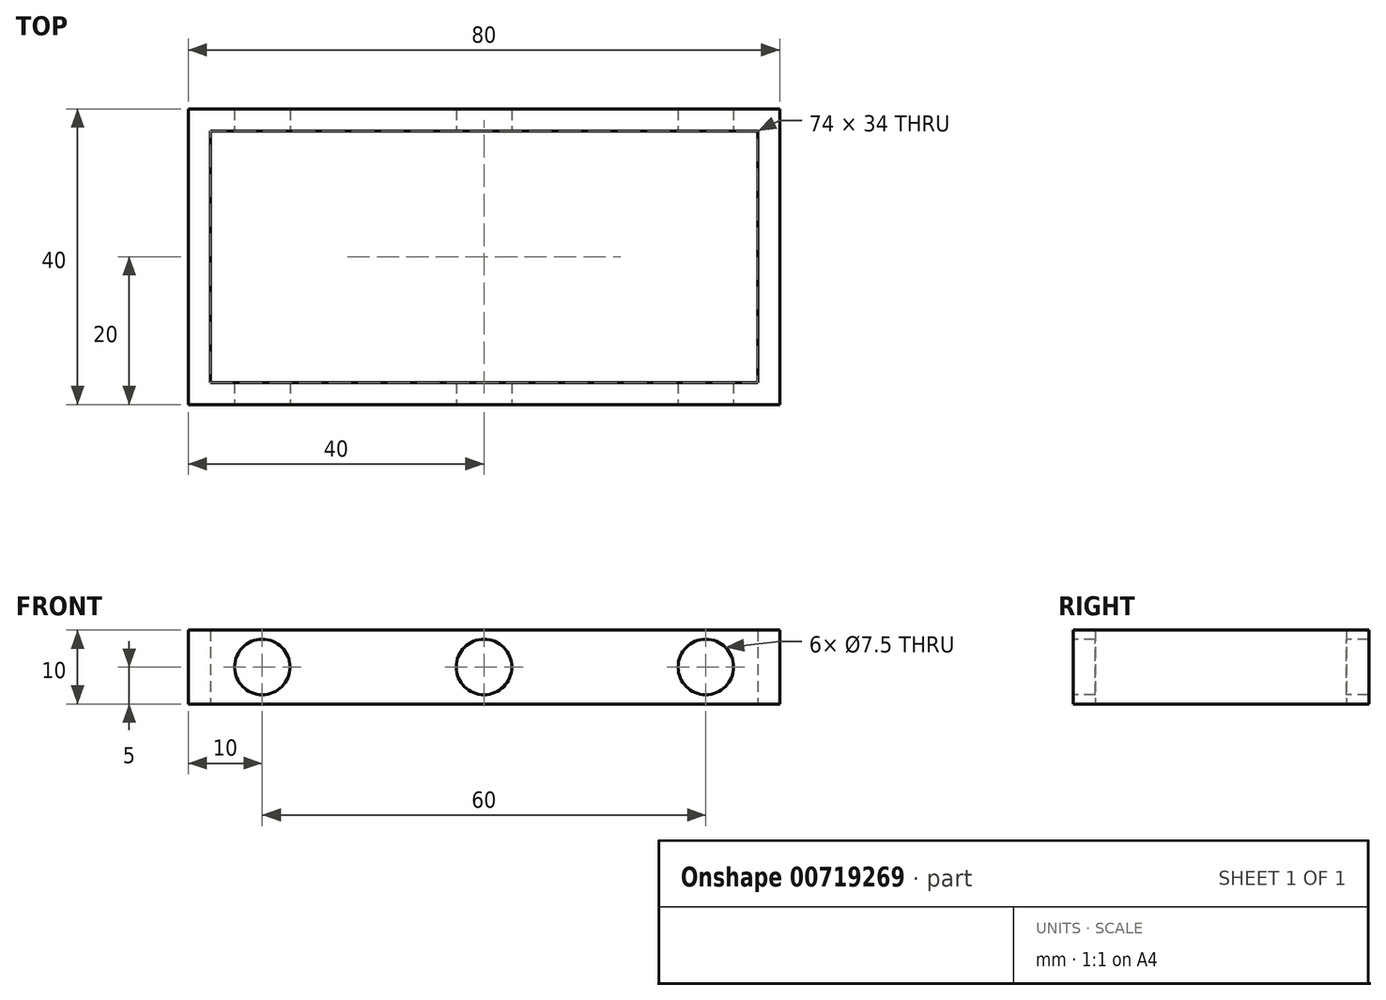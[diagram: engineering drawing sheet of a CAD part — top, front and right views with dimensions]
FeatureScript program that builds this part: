
annotation { "Feature Type Name" : "Feature", "Feature Type Description" : "" }
export const myFeature = defineFeature(function(context is Context, id is Id, definition is map)
    precondition{}
    {
        {
            var Q0;
            Q0=qCreatedBy(makeId("Front.planeOp"),FACE);
            var sketch = newSketch(context, id + "F0", { "sketchPlane" : qUnion([Q0])});
            skLineSegment(sketch, "E0.bottom", {"start": v(-40, 5) * mm, "end": v(40, 5) * mm});
            skLineSegment(sketch, "E0.top", {"start": v(-40, -5) * mm, "end": v(40, -5) * mm});
            skLineSegment(sketch, "E0.left", {"start": v(-40, 5) * mm, "end": v(-40, -5) * mm});
            skLineSegment(sketch, "E0.right", {"start": v(40, 5) * mm, "end": v(40, -5) * mm});
            skSolve(sketch);
        }
        {
            var Q0;
            Q0=makeQuery(id+"F0.imprint","IMPRINT",FACE,{"disambiguationData":[TD([[makeQuery(id+"F0.imprint","IMPRINT",EDGE,{"derivedFrom":sQuery(id+"F0.wireOp",EDGE,"E0.bottom")}),-1.0]])]});
            extrude(context, id + "F1", {"entities" : qUnion([Q0]), "depth" : 40 * mm, "offsetDistance" : 25 * mm, "symmetric" : true});
        }
        {
            var Q0;
            Q0=makeQuery(id+"F1.opExtrude","SWEPT_FACE",FACE,{"disambiguationData":[OSD([sQuery(id+"F0.wireOp",EDGE,"E0.bottom")])]});
            var Q1;
            Q1=makeQuery(id+"F1.opExtrude","SWEPT_FACE",FACE,{"disambiguationData":[OSD([sQuery(id+"F0.wireOp",EDGE,"E0.top")])]});
            shell(context, id + "F2", {"entities" : qUnion([Q0, Q1]), "thickness" : 3 * mm});
        }
        {
            var Q0;
            Q0=qCreatedBy(makeId("Front.planeOp"),FACE);
            var sketch = newSketch(context, id + "F3", { "sketchPlane" : qUnion([Q0])});
            skCircle(sketch, "E1", {"center": v(-30, 0) * mm, "radius": 3.75 * mm});
            skCircle(sketch, "E2", {"center": v(0, 0) * mm, "radius": 3.75 * mm});
            skCircle(sketch, "E3", {"center": v(30, 0) * mm, "radius": 3.75 * mm});
            skSolve(sketch);
        }
        {
            var Q0;
            Q0=makeQuery(id+"F3.imprint","IMPRINT",FACE,{"disambiguationData":[TD([[makeQuery(id+"F3.imprint","IMPRINT",EDGE,{"derivedFrom":sQuery(id+"F3.wireOp",EDGE,"E1")}),1.0]])]});
            var Q1;
            Q1=makeQuery(id+"F3.imprint","IMPRINT",FACE,{"disambiguationData":[TD([[makeQuery(id+"F3.imprint","IMPRINT",EDGE,{"derivedFrom":sQuery(id+"F3.wireOp",EDGE,"E2")}),1.0]])]});
            var Q2;
            Q2=makeQuery(id+"F3.imprint","IMPRINT",FACE,{"disambiguationData":[TD([[makeQuery(id+"F3.imprint","IMPRINT",EDGE,{"derivedFrom":sQuery(id+"F3.wireOp",EDGE,"E3")}),1.0]])]});
            extrude(context, id + "F4", {"entities" : qUnion([Q0, Q1, Q2]), "operationType" : NewBodyOperationType.REMOVE, "oppositeDirection" : true, "depth" : 50 * mm, "offsetDistance" : 25 * mm, "symmetric" : true});
        }
    });
